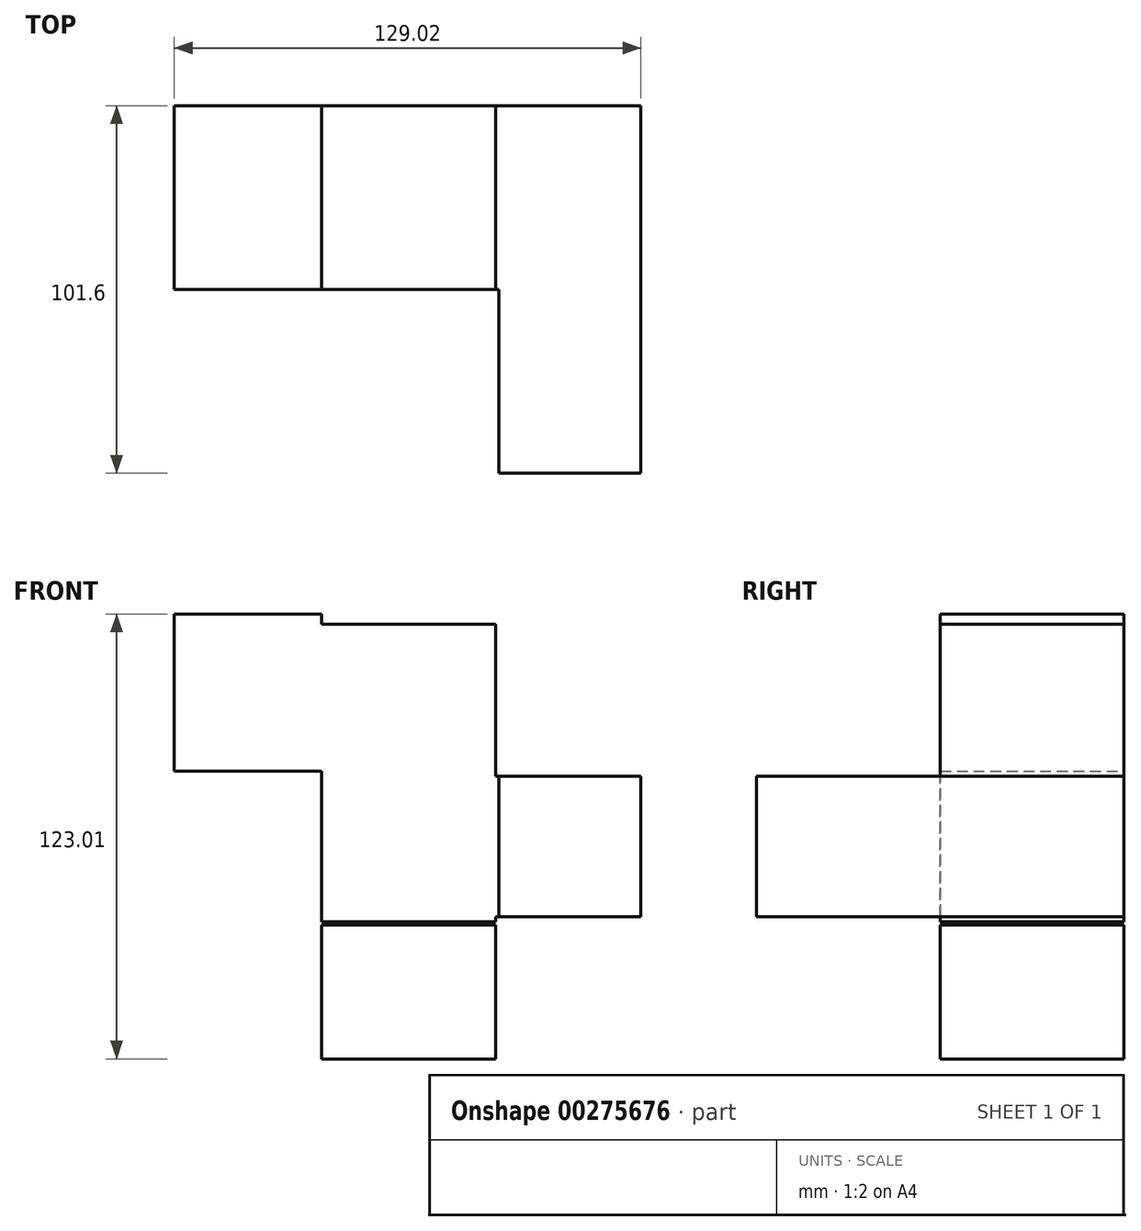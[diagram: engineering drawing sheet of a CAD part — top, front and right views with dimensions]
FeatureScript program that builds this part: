
annotation { "Feature Type Name" : "Feature", "Feature Type Description" : "" }
export const myFeature = defineFeature(function(context is Context, id is Id, definition is map)
    precondition{}
    {
        {
            var Q0;
            Q0=qCreatedBy(makeId("Front.planeOp"),FACE);
            var sketch = newSketch(context, id + "F0", { "sketchPlane" : qUnion([Q0])});
            skLineSegment(sketch, "E0.bottom", {"start": v(-24.05, 20.81) * mm, "end": v(24.05, 20.81) * mm});
            skLineSegment(sketch, "E0.top", {"start": v(-24.05, -20.81) * mm, "end": v(24.05, -20.81) * mm});
            skLineSegment(sketch, "E0.left", {"start": v(-24.05, 20.81) * mm, "end": v(-24.05, -20.81) * mm});
            skLineSegment(sketch, "E0.right", {"start": v(24.05, 20.81) * mm, "end": v(24.05, -20.81) * mm});
            skPoint(sketch, "E0.middle", {"position": v(0, 0) * mm});
            skLineSegment(sketch, "E1.bottom", {"start": v(24.05, 20.81) * mm, "end": v(-24.05, 20.81) * mm});
            skLineSegment(sketch, "E1.top", {"start": v(24.05, 61.5) * mm, "end": v(-24.05, 61.5) * mm});
            skLineSegment(sketch, "E1.left", {"start": v(24.05, 20.81) * mm, "end": v(24.05, 61.5) * mm});
            skLineSegment(sketch, "E1.right", {"start": v(-24.05, 20.81) * mm, "end": v(-24.05, 61.5) * mm});
            skPoint(sketch, "E1.middle", {"position": v(0, 41.16) * mm});
            skLineSegment(sketch, "E2.bottom", {"start": v(24.05, -58.73) * mm, "end": v(-24.05, -58.73) * mm});
            skLineSegment(sketch, "E2.top", {"start": v(24.05, -21.74) * mm, "end": v(-24.05, -21.74) * mm});
            skLineSegment(sketch, "E2.left", {"start": v(24.05, -58.73) * mm, "end": v(24.05, -21.74) * mm});
            skLineSegment(sketch, "E2.right", {"start": v(-24.05, -58.73) * mm, "end": v(-24.05, -21.74) * mm});
            skPoint(sketch, "E2.middle", {"position": v(0, -40.23) * mm});
            skLineSegment(sketch, "E3.bottom", {"start": v(-24.05, 20.81) * mm, "end": v(-64.74, 20.81) * mm});
            skLineSegment(sketch, "E3.top", {"start": v(-24.05, 64.28) * mm, "end": v(-64.74, 64.28) * mm});
            skLineSegment(sketch, "E3.left", {"start": v(-24.05, 20.81) * mm, "end": v(-24.05, 64.28) * mm});
            skLineSegment(sketch, "E3.right", {"start": v(-64.74, 20.81) * mm, "end": v(-64.74, 64.28) * mm});
            skPoint(sketch, "E3.middle", {"position": v(-44.4, 42.55) * mm});
            skLineSegment(sketch, "E4.bottom", {"start": v(64.28, -19.42) * mm, "end": v(23.59, -19.42) * mm});
            skLineSegment(sketch, "E4.top", {"start": v(64.28, 19.42) * mm, "end": v(23.59, 19.42) * mm});
            skLineSegment(sketch, "E4.left", {"start": v(64.28, -19.42) * mm, "end": v(64.28, 19.42) * mm});
            skLineSegment(sketch, "E4.right", {"start": v(23.59, -19.42) * mm, "end": v(23.59, 19.42) * mm});
            skPoint(sketch, "E4.middle", {"position": v(43.93, 0) * mm});
            skSolve(sketch);
        }
        {
            var Q0;
            Q0 = qSketchRegion(id + "F0", true);
            extrude(context, id + "F1", {"entities" : qUnion([Q0]), "depth" : 50.8 * mm});
        }
        {
            var Q0;
            Q0=makeQuery(id+"F1.opExtrude","CAP_FACE",FACE,{"disambiguationData":[OSD([sQuery(id+"F0.wireOp",EDGE,"E0.top"),sQuery(id+"F0.wireOp",EDGE,"E0.left"),sQuery(id+"F0.wireOp",EDGE,"E0.right"),sQuery(id+"F0.wireOp",EDGE,"E1.top"),sQuery(id+"F0.wireOp",EDGE,"E1.left"),sQuery(id+"F0.wireOp",EDGE,"E3.bottom"),sQuery(id+"F0.wireOp",EDGE,"E3.top"),sQuery(id+"F0.wireOp",EDGE,"E3.left"),sQuery(id+"F0.wireOp",EDGE,"E3.right"),sQuery(id+"F0.wireOp",EDGE,"E4.bottom"),sQuery(id+"F0.wireOp",EDGE,"E4.top"),sQuery(id+"F0.wireOp",EDGE,"E4.left")])],"isStart":false});
            var sketch = newSketch(context, id + "F2", { "sketchPlane" : qUnion([Q0])});
            skLineSegment(sketch, "E5.bottom", {"start": v(64.28, -19.42) * mm, "end": v(25.01, -19.42) * mm});
            skLineSegment(sketch, "E5.top", {"start": v(64.28, 19.42) * mm, "end": v(25.01, 19.42) * mm});
            skLineSegment(sketch, "E5.left", {"start": v(64.28, -19.42) * mm, "end": v(64.28, 19.42) * mm});
            skLineSegment(sketch, "E5.right", {"start": v(25.01, -19.42) * mm, "end": v(25.01, 19.42) * mm});
            skPoint(sketch, "E5.middle", {"position": v(44.65, 0) * mm});
            skSolve(sketch);
        }
        {
            var Q0;
            Q0 = qSketchRegion(id + "F2", true);
            extrude(context, id + "F3", {"entities" : qUnion([Q0]), "operationType" : NewBodyOperationType.ADD, "depth" : 50.8 * mm});
        }
    });
